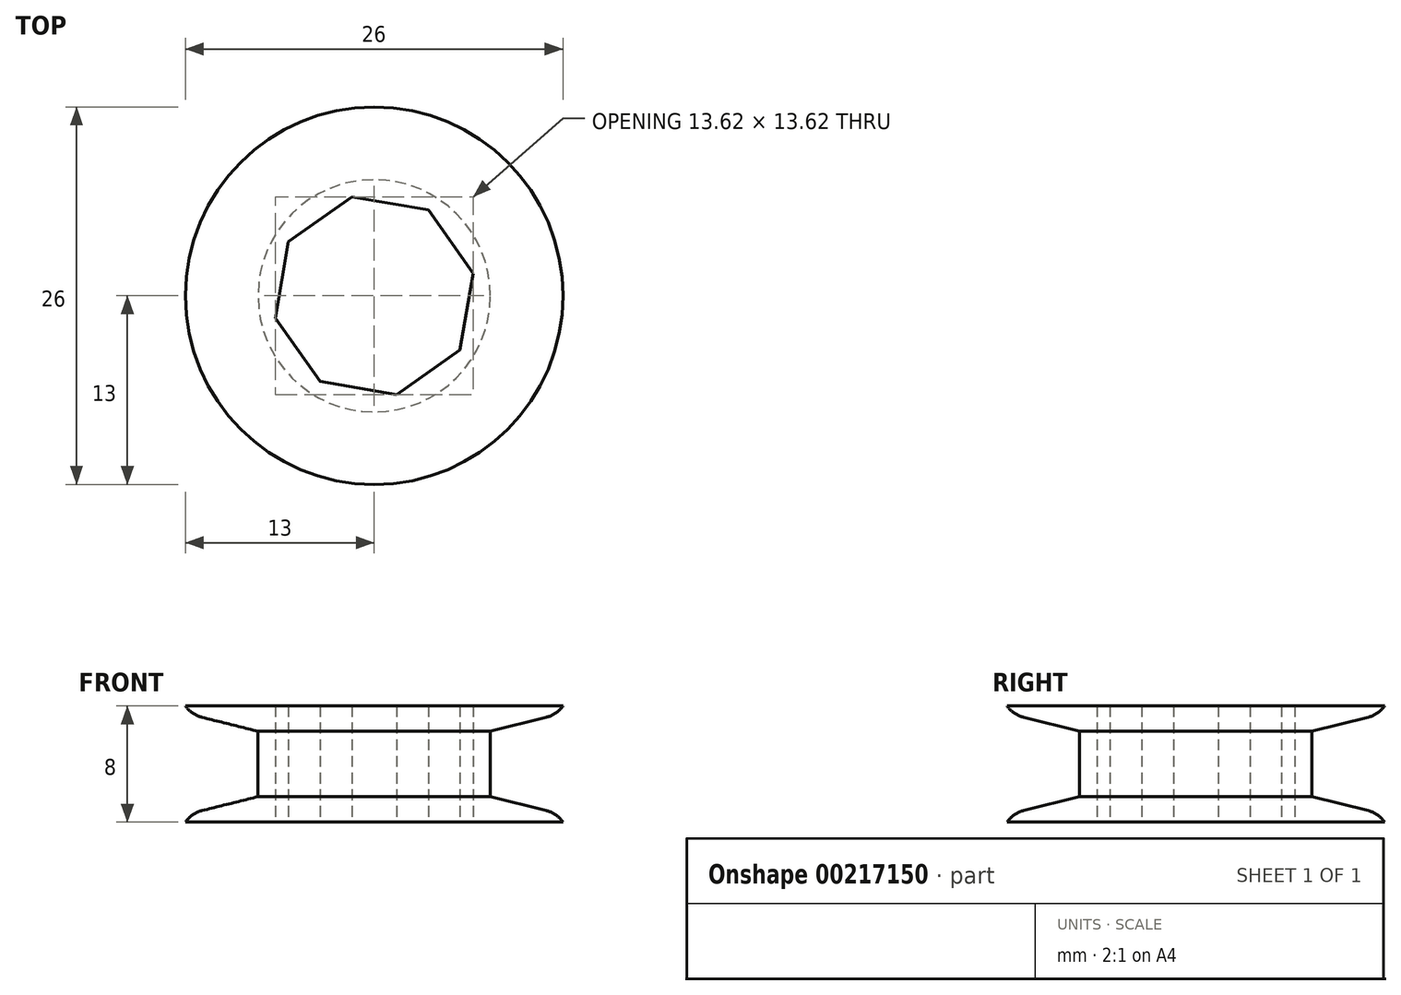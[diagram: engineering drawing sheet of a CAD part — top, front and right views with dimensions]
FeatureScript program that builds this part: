
annotation { "Feature Type Name" : "Feature", "Feature Type Description" : "" }
export const myFeature = defineFeature(function(context is Context, id is Id, definition is map)
    precondition{}
    {
        {
            var Q0;
            Q0=qCreatedBy(makeId("Front.planeOp"),FACE);
            var sketch = newSketch(context, id + "F0", { "sketchPlane" : qUnion([Q0])});
            skLineSegment(sketch, "E0.bottom", {"start": v(0, 0) * mm, "end": v(-13, 0) * mm});
            skLineSegment(sketch, "E0.top", {"start": v(0, 8) * mm, "end": v(-13, 8) * mm});
            skLineSegment(sketch, "E0.left", {"start": v(0, 0) * mm, "end": v(0, 8) * mm});
            skLineSegment(sketch, "E0.right", {"start": v(-13, 0) * mm, "end": v(-13, 0.5) * mm});
            skLineSegment(sketch, "E1", {"start": v(-13, 0.5) * mm, "end": v(-8, 1.75) * mm});
            skLineSegment(sketch, "E2", {"start": v(-21.75, 4) * mm, "end": v(9.2, 4) * mm, "construction": true});
            skLineSegment(sketch, "E3.MirrorCS", {"start": v(-13, 7.5) * mm, "end": v(-8, 6.25) * mm});
            skLineSegment(sketch, "E4", {"start": v(-8, 6.25) * mm, "end": v(-8, 1.75) * mm});
            skLineSegment(sketch, "E5.trimOffspring", {"start": v(-13, 7.5) * mm, "end": v(-13, 8) * mm});
            skSolve(sketch);
        }
        {
            var Q0;
            Q0=makeQuery(id+"F0.imprint","IMPRINT",FACE,{"disambiguationData":[TD([[makeQuery(id+"F0.imprint","IMPRINT",EDGE,{"derivedFrom":sQuery(id+"F0.wireOp",EDGE,"E0.bottom")}),-1.0]])]});
            var Q1;
            Q1=sQuery(id+"F0.wireOp",EDGE,"E0.left");
            revolve(context, id + "F1", {"entities" : qUnion([Q0]), "axis" : qUnion([Q1]), "revolveType" : RevolveType.FULL});
        }
        {
            var Q0;
            Q0=makeQuery(id+"F1.opRevolve","SWEPT_EDGE",EDGE,{"disambiguationData":[OSD([sQuery(id+"F0.wireOp",EDGE,"E3.MirrorCS"),sQuery(id+"F0.wireOp",EDGE,"E5.trimOffspring")])]});
            var Q1;
            Q1=makeQuery(id+"F1.opRevolve","SWEPT_EDGE",EDGE,{"disambiguationData":[OSD([sQuery(id+"F0.wireOp",EDGE,"E0.right"),sQuery(id+"F0.wireOp",EDGE,"E1")])]});
            fillet(context, id + "F2", {"entities" : qUnion([Q0, Q1]), "radius" : 2 * mm, "tangentPropagation" : true, "allowEdgeOverflow" : false});
        }
        {
            var Q0;
            Q0=qCreatedBy(makeId("Top.planeOp"),FACE);
            var sketch = newSketch(context, id + "F3", { "sketchPlane" : qUnion([Q0])});
            skCircle(sketch, "E6", {"center": v(0, 0) * mm, "radius": 6.45 * mm, "construction": true});
            skLineSegment(sketch, "E7.0", {"start": v(3.72, 5.9) * mm, "end": v(6.8, 1.54) * mm});
            skLineSegment(sketch, "E7.1", {"start": v(6.8, 1.54) * mm, "end": v(5.9, -3.72) * mm});
            skLineSegment(sketch, "E7.2", {"start": v(5.9, -3.72) * mm, "end": v(1.54, -6.8) * mm});
            skLineSegment(sketch, "E7.3", {"start": v(1.54, -6.8) * mm, "end": v(-3.72, -5.9) * mm});
            skLineSegment(sketch, "E7.4", {"start": v(-3.72, -5.9) * mm, "end": v(-6.8, -1.54) * mm});
            skLineSegment(sketch, "E7.5", {"start": v(-6.8, -1.54) * mm, "end": v(-5.9, 3.72) * mm});
            skLineSegment(sketch, "E7.6", {"start": v(-5.9, 3.72) * mm, "end": v(-1.54, 6.8) * mm});
            skLineSegment(sketch, "E7.7", {"start": v(-1.54, 6.8) * mm, "end": v(3.72, 5.9) * mm});
            skPoint(sketch, "E7.0.midPoint", {"position": v(5.27, 3.73) * mm});
            skSolve(sketch);
        }
        {
            var Q0;
            Q0=makeQuery(id+"F3.imprint","IMPRINT",FACE,{"disambiguationData":[TD([[makeQuery(id+"F3.imprint","IMPRINT",EDGE,{"derivedFrom":sQuery(id+"F3.wireOp",EDGE,"E7.0")}),-1.0]])]});
            extrude(context, id + "F4", {"entities" : qUnion([Q0]), "operationType" : NewBodyOperationType.REMOVE, "endBound" : BoundingType.THROUGH_ALL, "depth" : 25 * mm});
        }
    });
